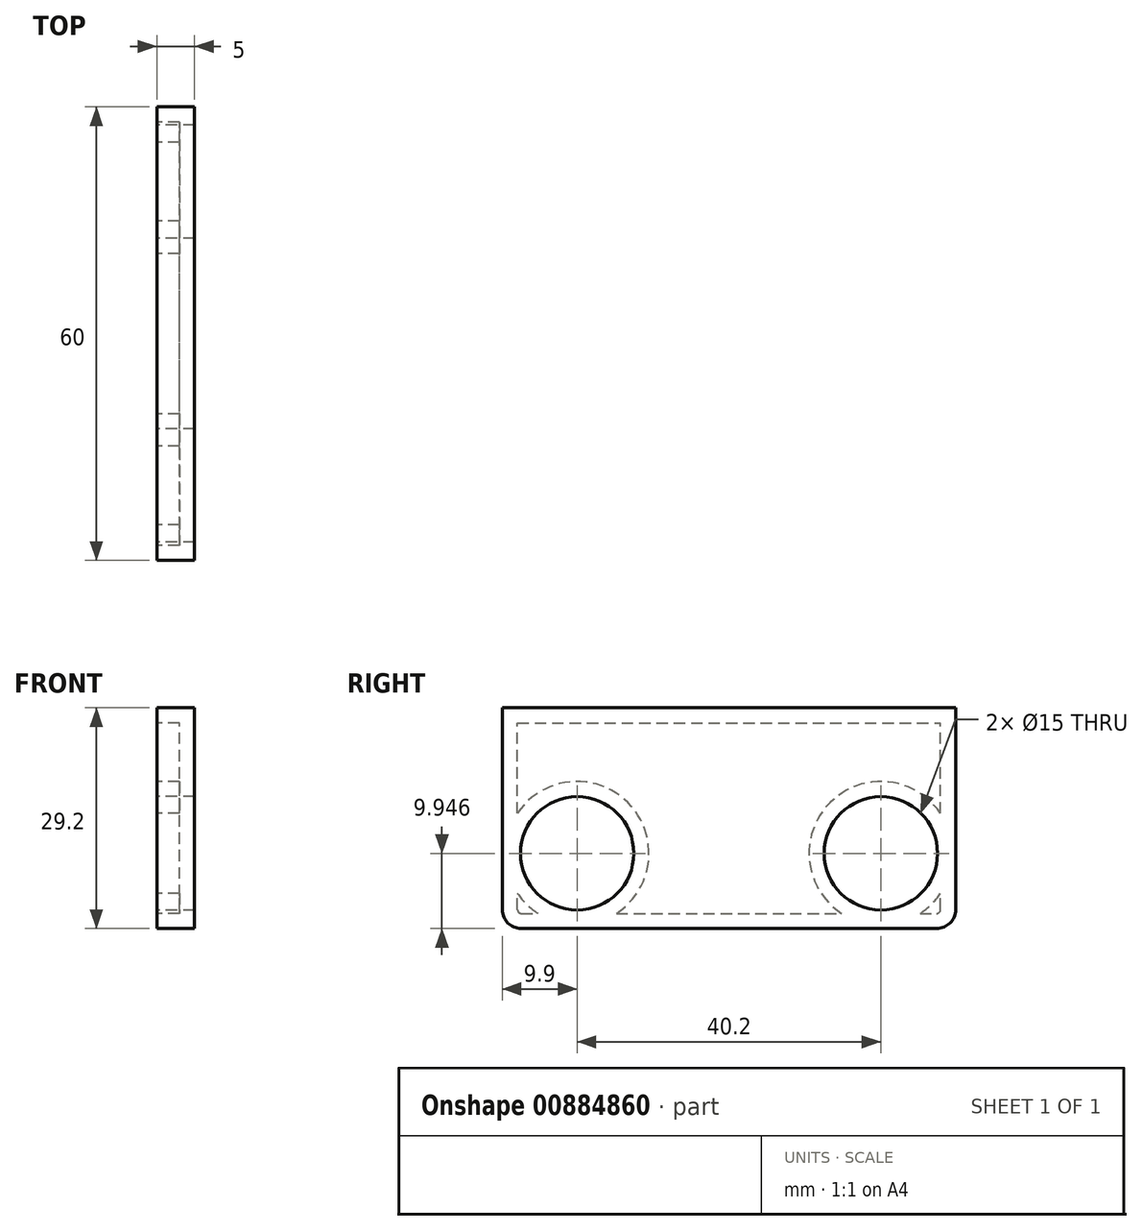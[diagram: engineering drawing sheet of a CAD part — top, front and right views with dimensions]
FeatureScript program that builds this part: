
annotation { "Feature Type Name" : "Feature", "Feature Type Description" : "" }
export const myFeature = defineFeature(function(context is Context, id is Id, definition is map)
    precondition{}
    {
        {
            var Q0;
            Q0=qCreatedBy(makeId("Right.planeOp"),FACE);
            var sketch = newSketch(context, id + "F0", { "sketchPlane" : qUnion([Q0])});
            skLineSegment(sketch, "E0.0", {"start": v(21.2, 3.44) * mm, "end": v(21.2, -21.26) * mm});
            skArc(sketch, "E0.1", {"start": v(20.2, -22.26) * mm, "mid": v(20.9, -21.96) * mm, "end": v(21.2, -21.26) * mm});
            skLineSegment(sketch, "E0.2", {"start": v(20.2, -22.26) * mm, "end": v(17.2, -22.26) * mm});
            skArc(sketch, "E0.3", {"start": v(16.2, -21.26) * mm, "mid": v(16.5, -21.96) * mm, "end": v(17.2, -22.26) * mm});
            skLineSegment(sketch, "E0.4", {"start": v(16.2, -7.6) * mm, "end": v(16.2, -21.26) * mm});
            skArc(sketch, "E0.5", {"start": v(15.47, -5.82) * mm, "mid": v(16.01, -6.64) * mm, "end": v(16.2, -7.6) * mm});
            skLineSegment(sketch, "E0.6", {"start": v(15.47, -5.82) * mm, "end": v(14.5, -4.85) * mm});
            skLineSegment(sketch, "E0.7", {"start": v(6.93, 2.71) * mm, "end": v(14.5, -4.85) * mm});
            skArc(sketch, "E0.8", {"start": v(5.17, 3.44) * mm, "mid": v(6.12, 3.25) * mm, "end": v(6.93, 2.71) * mm});
            skLineSegment(sketch, "E0.9", {"start": v(5.17, 3.44) * mm, "end": v(-1.3, 3.44) * mm});
            skArc(sketch, "E0.10", {"start": v(-3.8, 5.94) * mm, "mid": v(-3.07, 4.18) * mm, "end": v(-1.3, 3.44) * mm});
            skLineSegment(sketch, "E0.11", {"start": v(-3.8, 5.94) * mm, "end": v(-3.8, 10.94) * mm});
            skArc(sketch, "E0.12", {"start": v(-1.3, 13.44) * mm, "mid": v(-3.07, 12.71) * mm, "end": v(-3.8, 10.94) * mm});
            skLineSegment(sketch, "E0.13", {"start": v(15.2, 13.44) * mm, "end": v(-1.3, 13.44) * mm});
            skLineSegment(sketch, "E0.14", {"start": v(15.2, 13.44) * mm, "end": v(26.88, 13.44) * mm});
            skArc(sketch, "E0.15", {"start": v(29.24, 15.1) * mm, "mid": v(28.32, 13.9) * mm, "end": v(26.88, 13.44) * mm});
            skArc(sketch, "E0.16", {"start": v(35.62, 8.73) * mm, "mid": v(37.49, 16.98) * mm, "end": v(29.24, 15.1) * mm});
            skArc(sketch, "E0.17", {"start": v(33.95, 6.37) * mm, "mid": v(34.4, 7.82) * mm, "end": v(35.62, 8.73) * mm});
            skLineSegment(sketch, "E0.18", {"start": v(33.95, 6.37) * mm, "end": v(33.95, -5.34) * mm});
            skLineSegment(sketch, "E0.19", {"start": v(33.95, -5.34) * mm, "end": v(33.95, -14.06) * mm});
            skArc(sketch, "E0.20", {"start": v(31.45, -16.56) * mm, "mid": v(33.22, -15.82) * mm, "end": v(33.95, -14.06) * mm});
            skLineSegment(sketch, "E0.21", {"start": v(31.45, -16.56) * mm, "end": v(27.25, -16.56) * mm});
            skArc(sketch, "E0.22", {"start": v(24.75, -14.06) * mm, "mid": v(25.48, -15.82) * mm, "end": v(27.25, -16.56) * mm});
            skLineSegment(sketch, "E0.23", {"start": v(24.75, -5.34) * mm, "end": v(24.75, -14.06) * mm});
            skLineSegment(sketch, "E0.24", {"start": v(24.75, 3.44) * mm, "end": v(24.75, -5.34) * mm});
            skLineSegment(sketch, "E1", {"start": v(21.2, 3.44) * mm, "end": v(24.75, 3.44) * mm});
            skLineSegment(sketch, "E2.0", {"start": v(12.45, 11.2) * mm, "end": v(12.45, 4.44) * mm});
            skLineSegment(sketch, "E2.1", {"start": v(12.45, 4.44) * mm, "end": v(-1.05, 4.44) * mm});
            skLineSegment(sketch, "E2.2", {"start": v(-1.05, 11.2) * mm, "end": v(-1.05, 4.44) * mm});
            skLineSegment(sketch, "E2.3", {"start": v(-1.05, 11.2) * mm, "end": v(12.45, 11.2) * mm});
            skSolve(sketch);
        }
        {
            var Q0;
            Q0 = qSketchRegion(id + "F0", true);
            extrude(context, id + "F1", {"entities" : qUnion([Q0]), "depth" : 20 * mm, "offsetDistance" : 25 * mm});
        }
        {
            var Q0;
            Q0=makeQuery(id+"F1.opExtrude","CAP_FACE",FACE,{"disambiguationData":[OSD([sQuery(id+"F0.wireOp",EDGE,"E0.0"),sQuery(id+"F0.wireOp",EDGE,"E0.1"),sQuery(id+"F0.wireOp",EDGE,"E0.2"),sQuery(id+"F0.wireOp",EDGE,"E0.3"),sQuery(id+"F0.wireOp",EDGE,"E0.4"),sQuery(id+"F0.wireOp",EDGE,"E0.5"),sQuery(id+"F0.wireOp",EDGE,"E0.6"),sQuery(id+"F0.wireOp",EDGE,"E0.7"),sQuery(id+"F0.wireOp",EDGE,"E0.8"),sQuery(id+"F0.wireOp",EDGE,"E0.9"),sQuery(id+"F0.wireOp",EDGE,"E0.10"),sQuery(id+"F0.wireOp",EDGE,"E0.11"),sQuery(id+"F0.wireOp",EDGE,"E0.12"),sQuery(id+"F0.wireOp",EDGE,"E0.13"),sQuery(id+"F0.wireOp",EDGE,"E0.14"),sQuery(id+"F0.wireOp",EDGE,"E0.15"),sQuery(id+"F0.wireOp",EDGE,"E0.16"),sQuery(id+"F0.wireOp",EDGE,"E0.17"),sQuery(id+"F0.wireOp",EDGE,"E0.18"),sQuery(id+"F0.wireOp",EDGE,"E0.19"),sQuery(id+"F0.wireOp",EDGE,"E0.20"),sQuery(id+"F0.wireOp",EDGE,"E0.21"),sQuery(id+"F0.wireOp",EDGE,"E0.22"),sQuery(id+"F0.wireOp",EDGE,"E0.23"),sQuery(id+"F0.wireOp",EDGE,"E0.24"),sQuery(id+"F0.wireOp",EDGE,"E1"),sQuery(id+"F0.wireOp",EDGE,"E2.0"),sQuery(id+"F0.wireOp",EDGE,"E2.1"),sQuery(id+"F0.wireOp",EDGE,"E2.2"),sQuery(id+"F0.wireOp",EDGE,"E2.3")])],"isStart":false});
            var sketch = newSketch(context, id + "F2", { "sketchPlane" : qUnion([Q0])});
            skLineSegment(sketch, "E3.bottom", {"start": v(9.7, 24.43) * mm, "end": v(1.7, 24.43) * mm});
            skLineSegment(sketch, "E3.top", {"start": v(9.7, -2.04) * mm, "end": v(1.7, -2.04) * mm});
            skLineSegment(sketch, "E3.left", {"start": v(9.7, 24.43) * mm, "end": v(9.7, -2.04) * mm});
            skLineSegment(sketch, "E3.right", {"start": v(1.7, 24.43) * mm, "end": v(1.7, -2.04) * mm});
            skPoint(sketch, "E3.middle", {"position": v(5.7, 11.2) * mm});
            skSolve(sketch);
        }
        {
            var Q0;
            Q0 = qSketchRegion(id + "F2", true);
            extrude(context, id + "F3", {"entities" : qUnion([Q0]), "operationType" : NewBodyOperationType.REMOVE, "oppositeDirection" : true, "depth" : 12 * mm, "offsetDistance" : 25 * mm});
        }
        {
            var Q0;
            Q0=makeQuery(id+"F3.boolean.opBoolean","INTERSECT",EDGE,{"derivedFrom":[makeQuery(id+"F1.opExtrude","SWEPT_FACE",FACE,{"disambiguationData":[OSD([sQuery(id+"F0.wireOp",EDGE,"E2.3")])]}),makeQuery(id+"F3.opExtrude","SWEPT_FACE",FACE,{"disambiguationData":[OSD([sQuery(id+"F2.wireOp",EDGE,"E3.right")])]})]});
            var Q1;
            Q1=makeQuery(id+"F3.boolean.opBoolean","INTERSECT",EDGE,{"derivedFrom":[makeQuery(id+"F1.opExtrude","SWEPT_FACE",FACE,{"disambiguationData":[OSD([sQuery(id+"F0.wireOp",EDGE,"E0.13"),sQuery(id+"F0.wireOp",EDGE,"E0.14")])]}),makeQuery(id+"F3.opExtrude","SWEPT_FACE",FACE,{"disambiguationData":[OSD([sQuery(id+"F2.wireOp",EDGE,"E3.right")])]})]});
            var Q2;
            Q2=makeQuery(id+"F3.boolean.opBoolean","INTERSECT",EDGE,{"derivedFrom":[makeQuery(id+"F1.opExtrude","SWEPT_FACE",FACE,{"disambiguationData":[OSD([sQuery(id+"F0.wireOp",EDGE,"E2.1")])]}),makeQuery(id+"F3.opExtrude","SWEPT_FACE",FACE,{"disambiguationData":[OSD([sQuery(id+"F2.wireOp",EDGE,"E3.right")])]})]});
            var Q3;
            Q3=makeQuery(id+"F3.boolean.opBoolean","INTERSECT",EDGE,{"derivedFrom":[makeQuery(id+"F1.opExtrude","SWEPT_FACE",FACE,{"disambiguationData":[OSD([sQuery(id+"F0.wireOp",EDGE,"E0.9")])]}),makeQuery(id+"F3.opExtrude","SWEPT_FACE",FACE,{"disambiguationData":[OSD([sQuery(id+"F2.wireOp",EDGE,"E3.right")])]})]});
            var Q4;
            Q4=makeQuery(id+"F1.opExtrude","SWEPT_EDGE",EDGE,{"disambiguationData":[OSD([sQuery(id+"F0.wireOp",EDGE,"E2.1"),sQuery(id+"F0.wireOp",EDGE,"E2.2")])]});
            var Q5;
            Q5=makeQuery(id+"F1.opExtrude","SWEPT_EDGE",EDGE,{"disambiguationData":[OSD([sQuery(id+"F0.wireOp",EDGE,"E2.2"),sQuery(id+"F0.wireOp",EDGE,"E2.3")])]});
            var Q6;
            Q6=makeQuery(id+"F1.opExtrude","SWEPT_EDGE",EDGE,{"disambiguationData":[OSD([sQuery(id+"F0.wireOp",EDGE,"E2.0"),sQuery(id+"F0.wireOp",EDGE,"E2.3")])]});
            var Q7;
            Q7=makeQuery(id+"F1.opExtrude","SWEPT_EDGE",EDGE,{"disambiguationData":[OSD([sQuery(id+"F0.wireOp",EDGE,"E2.0"),sQuery(id+"F0.wireOp",EDGE,"E2.1")])]});
            var Q8;
            Q8=makeQuery(id+"F3.boolean.opBoolean","INTERSECT",EDGE,{"derivedFrom":[makeQuery(id+"F1.opExtrude","SWEPT_FACE",FACE,{"disambiguationData":[OSD([sQuery(id+"F0.wireOp",EDGE,"E2.3")])]}),makeQuery(id+"F3.opExtrude","SWEPT_FACE",FACE,{"disambiguationData":[OSD([sQuery(id+"F2.wireOp",EDGE,"E3.left")])]})]});
            var Q9;
            Q9=makeQuery(id+"F3.boolean.opBoolean","INTERSECT",EDGE,{"derivedFrom":[makeQuery(id+"F1.opExtrude","SWEPT_FACE",FACE,{"disambiguationData":[OSD([sQuery(id+"F0.wireOp",EDGE,"E0.13"),sQuery(id+"F0.wireOp",EDGE,"E0.14")])]}),makeQuery(id+"F3.opExtrude","SWEPT_FACE",FACE,{"disambiguationData":[OSD([sQuery(id+"F2.wireOp",EDGE,"E3.left")])]})]});
            var Q10;
            Q10=makeQuery(id+"F3.boolean.opBoolean","INTERSECT",EDGE,{"derivedFrom":[makeQuery(id+"F1.opExtrude","SWEPT_FACE",FACE,{"disambiguationData":[OSD([sQuery(id+"F0.wireOp",EDGE,"E2.1")])]}),makeQuery(id+"F3.opExtrude","SWEPT_FACE",FACE,{"disambiguationData":[OSD([sQuery(id+"F2.wireOp",EDGE,"E3.left")])]})]});
            fillet(context, id + "F4", {"entities" : qUnion([Q0, Q1, Q2, Q3, Q4, Q5, Q6, Q7, Q8, Q9, Q10]), "radius" : 0.5 * mm, "tangentPropagation" : true, "allowEdgeOverflow" : false});
        }
        {
            var Q0;
            {var subQ0=sQuery(id+"F0.wireOp",EDGE,"E0.7");var subQ1=sQuery(id+"F0.wireOp",EDGE,"E0.6");var subQ2=sQuery(id+"F0.wireOp",EDGE,"E0.5");var subQ3=sQuery(id+"F0.wireOp",EDGE,"E0.4");var subQ4=sQuery(id+"F0.wireOp",EDGE,"E0.0");var subQ5=sQuery(id+"F0.wireOp",EDGE,"E1");var subQ6=sQuery(id+"F0.wireOp",EDGE,"E0.16");var subQ7=sQuery(id+"F0.wireOp",EDGE,"E0.3");var subQ8=sQuery(id+"F0.wireOp",EDGE,"E0.14");var subQ9=sQuery(id+"F0.wireOp",EDGE,"E0.13");var subQ10=sQuery(id+"F0.wireOp",EDGE,"E0.1");var subQ11=sQuery(id+"F0.wireOp",EDGE,"E0.15");var subQ12=sQuery(id+"F0.wireOp",EDGE,"E0.2");var subQ13=sQuery(id+"F0.wireOp",EDGE,"E2.3");var subQ14=sQuery(id+"F0.wireOp",EDGE,"E0.17");var subQ15=sQuery(id+"F0.wireOp",EDGE,"E0.19");var subQ16=sQuery(id+"F0.wireOp",EDGE,"E0.18");var subQ17=sQuery(id+"F0.wireOp",EDGE,"E0.20");var subQ18=sQuery(id+"F0.wireOp",EDGE,"E0.21");var subQ19=sQuery(id+"F0.wireOp",EDGE,"E0.22");var subQ20=sQuery(id+"F0.wireOp",EDGE,"E0.24");var subQ21=sQuery(id+"F0.wireOp",EDGE,"E0.23");var subQ22=sQuery(id+"F0.wireOp",EDGE,"E2.0");var subQ23=sQuery(id+"F0.wireOp",EDGE,"E2.1");Q0=makeQuery(id+"F3.boolean.opBoolean","SPLIT",FACE,{"disambiguationData":[TD([makeQuery(id+"F1.opExtrude","SWEPT_FACE",FACE,{"disambiguationData":[OSD([subQ4])]})])],"derivedFrom":makeQuery(id+"F1.opExtrude","CAP_FACE",FACE,{"disambiguationData":[OSD([subQ4,subQ10,subQ12,subQ7,subQ3,subQ2,subQ1,subQ0,sQuery(id+"F0.wireOp",EDGE,"E0.8"),sQuery(id+"F0.wireOp",EDGE,"E0.9"),sQuery(id+"F0.wireOp",EDGE,"E0.10"),sQuery(id+"F0.wireOp",EDGE,"E0.11"),sQuery(id+"F0.wireOp",EDGE,"E0.12"),subQ9,subQ8,subQ11,subQ6,subQ14,subQ16,subQ15,subQ17,subQ18,subQ19,subQ21,subQ20,subQ5,subQ22,subQ23,sQuery(id+"F0.wireOp",EDGE,"E2.2"),subQ13])],"isStart":false})});}
            shell(context, id + "F5", {"entities" : qUnion([Q0]), "thickness" : 2.5 * mm});
        }
        {
            var Q0;
            Q0=makeQuery(id+"F5.opShell","OFFSET_EDGE",EDGE,{"disambiguationData":[OSD([sQuery(id+"F0.wireOp",EDGE,"E0.4"),sQuery(id+"F0.wireOp",EDGE,"E0.5")])]});
            var Q1;
            Q1=makeQuery(id+"F5.opShell","TWEAK_EDGE",EDGE,{"derivedFrom":[makeQuery(id+"F1.opExtrude","SWEPT_FACE",FACE,{"disambiguationData":[OSD([sQuery(id+"F0.wireOp",EDGE,"E0.6"),sQuery(id+"F0.wireOp",EDGE,"E0.7")])]}),makeQuery(id+"F1.opExtrude","SWEPT_FACE",FACE,{"disambiguationData":[OSD([sQuery(id+"F0.wireOp",EDGE,"E2.1")])]})]});
            var Q2;
            Q2=makeQuery(id+"F5.opShell","OFFSET_EDGE",EDGE,{"disambiguationData":[OSD([sQuery(id+"F0.wireOp",EDGE,"E0.0"),sQuery(id+"F0.wireOp",EDGE,"E1")])]});
            var Q3;
            Q3=makeQuery(id+"F5.opShell","OFFSET_EDGE",EDGE,{"disambiguationData":[OSD([sQuery(id+"F0.wireOp",EDGE,"E0.24"),sQuery(id+"F0.wireOp",EDGE,"E1")])]});
            var Q4;
            Q4=makeQuery(id+"F5.opShell","TWEAK_EDGE",EDGE,{"derivedFrom":[makeQuery(id+"F4.opFillet","BLEND_FACE",FACE,{"disambiguationData":[OSD([sQuery(id+"F0.wireOp",EDGE,"E2.0"),sQuery(id+"F0.wireOp",EDGE,"E2.3")])]}),makeQuery(id+"F1.opExtrude","SWEPT_FACE",FACE,{"disambiguationData":[OSD([sQuery(id+"F0.wireOp",EDGE,"E0.13"),sQuery(id+"F0.wireOp",EDGE,"E0.14")])]})]});
            var Q5;
            Q5=makeQuery(id+"F5.opShell","OFFSET_EDGE",EDGE,{"disambiguationData":[OSD([sQuery(id+"F0.wireOp",EDGE,"E0.19"),sQuery(id+"F0.wireOp",EDGE,"E0.20"),sQuery(id+"F0.wireOp",EDGE,"E0.21")])]});
            var Q6;
            Q6=makeQuery(id+"F5.opShell","OFFSET_EDGE",EDGE,{"disambiguationData":[OSD([sQuery(id+"F0.wireOp",EDGE,"E0.21"),sQuery(id+"F0.wireOp",EDGE,"E0.22"),sQuery(id+"F0.wireOp",EDGE,"E0.23")])]});
            fillet(context, id + "F6", {"entities" : qUnion([Q0, Q1, Q2, Q3, Q4, Q5, Q6]), "radius" : 1 * mm, "tangentPropagation" : true, "allowEdgeOverflow" : false});
        }
        {
            var Q0;
            Q0=qCreatedBy(makeId("Right.planeOp"),FACE);
            var sketch = newSketch(context, id + "F7", { "sketchPlane" : qUnion([Q0])});
            skLineSegment(sketch, "E4.0", {"start": v(-22.61, 45.07) * mm, "end": v(-72.61, 45.07) * mm});
            skLineSegment(sketch, "E4.1", {"start": v(-22.61, 45.07) * mm, "end": v(2.14, 45.07) * mm, "construction": true});
            skLineSegment(sketch, "E4.2", {"start": v(-72.61, 45.07) * mm, "end": v(-97.36, 45.07) * mm, "construction": true});
            skLineSegment(sketch, "E4.3", {"start": v(-77.61, 27.57) * mm, "end": v(-77.61, 45.07) * mm});
            skArc(sketch, "E4.4", {"start": v(-77.61, 27.57) * mm, "mid": v(-76.88, 25.8) * mm, "end": v(-75.11, 25.07) * mm});
            skLineSegment(sketch, "E4.5", {"start": v(-75.11, 25.07) * mm, "end": v(-20.11, 25.07) * mm});
            skArc(sketch, "E4.6", {"start": v(-20.11, 25.07) * mm, "mid": v(-18.34, 25.8) * mm, "end": v(-17.61, 27.57) * mm});
            skLineSegment(sketch, "E4.7", {"start": v(-17.61, 27.57) * mm, "end": v(-17.61, 45.07) * mm});
            skCircle(sketch, "E5.0", {"center": v(-67.71, 35.02) * mm, "radius": 7.5 * mm});
            skCircle(sketch, "E5.1", {"center": v(-27.51, 35.02) * mm, "radius": 7.5 * mm});
            skLineSegment(sketch, "E6", {"start": v(-72.61, 45.07) * mm, "end": v(-77.61, 45.07) * mm, "construction": true});
            skLineSegment(sketch, "E7.bottom", {"start": v(-77.61, 45.07) * mm, "end": v(-17.61, 45.07) * mm});
            skLineSegment(sketch, "E7.top", {"start": v(-77.61, 54.27) * mm, "end": v(-17.61, 54.27) * mm});
            skLineSegment(sketch, "E7.left", {"start": v(-77.61, 45.07) * mm, "end": v(-77.61, 54.27) * mm});
            skLineSegment(sketch, "E7.right", {"start": v(-17.61, 45.07) * mm, "end": v(-17.61, 54.27) * mm});
            skSolve(sketch);
        }
        {
            var Q0;
            Q0 = qSketchRegion(id + "F7", true);
            extrude(context, id + "F8", {"entities" : qUnion([Q0]), "depth" : 5 * mm, "offsetDistance" : 25 * mm});
        }
        {
            var Q0;
            Q0=makeQuery(id+"F8.opExtrude","CAP_FACE",FACE,{"disambiguationData":[OSD([sQuery(id+"F7.wireOp",EDGE,"E4.3"),sQuery(id+"F7.wireOp",EDGE,"E4.4"),sQuery(id+"F7.wireOp",EDGE,"E4.5"),sQuery(id+"F7.wireOp",EDGE,"E4.6"),sQuery(id+"F7.wireOp",EDGE,"E4.7"),sQuery(id+"F7.wireOp",EDGE,"E5.0"),sQuery(id+"F7.wireOp",EDGE,"E5.1"),sQuery(id+"F7.wireOp",EDGE,"E7.top"),sQuery(id+"F7.wireOp",EDGE,"E7.left"),sQuery(id+"F7.wireOp",EDGE,"E7.right")])],"isStart":true});
            shell(context, id + "F9", {"entities" : qUnion([Q0]), "thickness" : 2 * mm});
        }
        {
            var Q0;
            Q0=makeQuery(id+"F1.opExtrude","SWEPT_BODY",BODY,{"disambiguationData":[OSD([sQuery(id+"F0.wireOp",EDGE,"E0.0"),sQuery(id+"F0.wireOp",EDGE,"E0.1"),sQuery(id+"F0.wireOp",EDGE,"E0.2"),sQuery(id+"F0.wireOp",EDGE,"E0.3"),sQuery(id+"F0.wireOp",EDGE,"E0.4"),sQuery(id+"F0.wireOp",EDGE,"E0.5"),sQuery(id+"F0.wireOp",EDGE,"E0.6"),sQuery(id+"F0.wireOp",EDGE,"E0.7"),sQuery(id+"F0.wireOp",EDGE,"E0.8"),sQuery(id+"F0.wireOp",EDGE,"E0.9"),sQuery(id+"F0.wireOp",EDGE,"E0.10"),sQuery(id+"F0.wireOp",EDGE,"E0.11"),sQuery(id+"F0.wireOp",EDGE,"E0.12"),sQuery(id+"F0.wireOp",EDGE,"E0.13"),sQuery(id+"F0.wireOp",EDGE,"E0.14"),sQuery(id+"F0.wireOp",EDGE,"E0.15"),sQuery(id+"F0.wireOp",EDGE,"E0.16"),sQuery(id+"F0.wireOp",EDGE,"E0.17"),sQuery(id+"F0.wireOp",EDGE,"E0.18"),sQuery(id+"F0.wireOp",EDGE,"E0.19"),sQuery(id+"F0.wireOp",EDGE,"E0.20"),sQuery(id+"F0.wireOp",EDGE,"E0.21"),sQuery(id+"F0.wireOp",EDGE,"E0.22"),sQuery(id+"F0.wireOp",EDGE,"E0.23"),sQuery(id+"F0.wireOp",EDGE,"E0.24"),sQuery(id+"F0.wireOp",EDGE,"E1"),sQuery(id+"F0.wireOp",EDGE,"E2.0"),sQuery(id+"F0.wireOp",EDGE,"E2.1"),sQuery(id+"F0.wireOp",EDGE,"E2.2"),sQuery(id+"F0.wireOp",EDGE,"E2.3")])]});
            deleteBodies(context, id + "F10", {"entities" : qUnion([Q0])});
        }
    });
